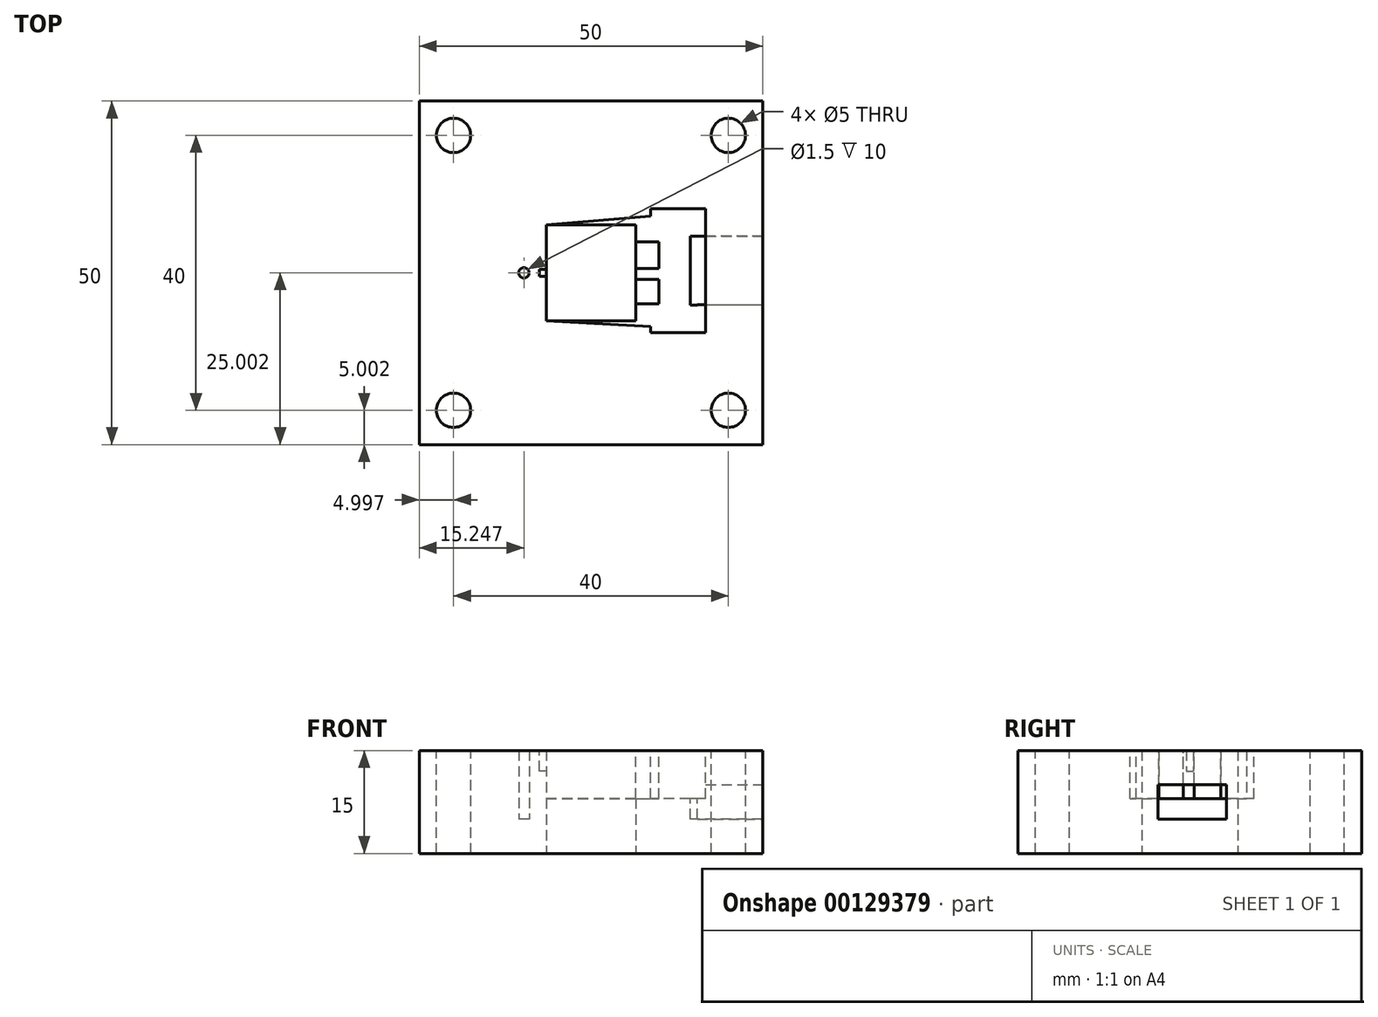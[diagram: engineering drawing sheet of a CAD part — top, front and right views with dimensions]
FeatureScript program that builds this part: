
annotation { "Feature Type Name" : "Feature", "Feature Type Description" : "" }
export const myFeature = defineFeature(function(context is Context, id is Id, definition is map)
    precondition{}
    {
        {
            var Q0;
            Q0=qCreatedBy(makeId("Top.planeOp"),FACE);
            var sketch = newSketch(context, id + "F0", { "sketchPlane" : qUnion([Q0])});
            skLineSegment(sketch, "E0.bottom", {"start": v(-16.2, 16.2) * mm, "end": v(23.8, 16.2) * mm});
            skLineSegment(sketch, "E0.top", {"start": v(-16.2, -23.8) * mm, "end": v(23.8, -23.8) * mm});
            skLineSegment(sketch, "E0.left", {"start": v(-16.2, 16.2) * mm, "end": v(-16.2, -23.8) * mm});
            skLineSegment(sketch, "E0.right", {"start": v(23.8, 16.2) * mm, "end": v(23.8, -23.8) * mm});
            skLineSegment(sketch, "E1", {"start": v(3.8, 16.2) * mm, "end": v(3.8, -23.8) * mm, "construction": true});
            skLineSegment(sketch, "E2", {"start": v(-16.2, -3.8) * mm, "end": v(23.8, -3.8) * mm, "construction": true});
            skLineSegment(sketch, "E3.bottom", {"start": v(10.3, -10.8) * mm, "end": v(-2.7, -10.8) * mm});
            skLineSegment(sketch, "E3.top", {"start": v(10.3, 3.2) * mm, "end": v(-2.7, 3.2) * mm});
            skLineSegment(sketch, "E3.left", {"start": v(10.3, -10.8) * mm, "end": v(10.3, 3.2) * mm});
            skLineSegment(sketch, "E3.right", {"start": v(-2.7, -10.8) * mm, "end": v(-2.7, 3.2) * mm});
            skPoint(sketch, "E3.middle", {"position": v(3.8, -3.8) * mm});
            skCircle(sketch, "E4", {"center": v(-5.95, -3.8) * mm, "radius": 0.75 * mm});
            skSolve(sketch);
        }
        {
            var Q0;
            Q0 = qSketchRegion(id + "F0", true);
            extrude(context, id + "F1", {"entities" : qUnion([Q0]), "depth" : 10 * mm});
        }
        {
            var Q0;
            Q0=makeQuery(id+"F1.opExtrude","CAP_FACE",FACE,{"disambiguationData":[OSD([sQuery(id+"F0.wireOp",EDGE,"E0.bottom"),sQuery(id+"F0.wireOp",EDGE,"E0.top"),sQuery(id+"F0.wireOp",EDGE,"E0.left"),sQuery(id+"F0.wireOp",EDGE,"E0.right"),sQuery(id+"F0.wireOp",EDGE,"E3.bottom"),sQuery(id+"F0.wireOp",EDGE,"E3.top"),sQuery(id+"F0.wireOp",EDGE,"E3.left"),sQuery(id+"F0.wireOp",EDGE,"E3.right")])],"isStart":false});
            var sketch = newSketch(context, id + "F2", { "sketchPlane" : qUnion([Q0])});
            skLineSegment(sketch, "E5", {"start": v(-2.7, -10.8) * mm, "end": v(19.32, -11.97) * mm});
            skLineSegment(sketch, "E6", {"start": v(-2.7, 3.2) * mm, "end": v(19.27, 5.03) * mm});
            skLineSegment(sketch, "E7", {"start": v(19.27, 5.03) * mm, "end": v(19.32, -11.97) * mm});
            skLineSegment(sketch, "E8", {"start": v(10.3, -1.44) * mm, "end": v(14.3, -1.44) * mm});
            skLineSegment(sketch, "E9", {"start": v(10.3, -5.36) * mm, "end": v(14.12, -5.36) * mm});
            skLineSegment(sketch, "E10", {"start": v(14.3, -5.36) * mm, "end": v(14.3, -1.44) * mm});
            skPoint(sketch, "E11.endSnap0", {"position": v(19.3, -3.47) * mm});
            skLineSegment(sketch, "E12", {"start": v(10.3, -1.44) * mm, "end": v(10.3, -5.36) * mm});
            skLineSegment(sketch, "E13", {"start": v(-2.7, -10.8) * mm, "end": v(-2.7, 3.2) * mm});
            skSolve(sketch);
        }
        {
            var Q0;
            Q0=makeQuery(id+"F2.imprint","IMPRINT",FACE,{"disambiguationData":[TD([[makeQuery(id+"F2.imprint","IMPRINT",EDGE,{"derivedFrom":sQuery(id+"F2.wireOp",EDGE,"E5")}),1.0]])]});
            extrude(context, id + "F3", {"entities" : qUnion([Q0]), "operationType" : NewBodyOperationType.REMOVE, "oppositeDirection" : true, "depth" : 7 * mm});
        }
        {
            var Q0;
            Q0=makeQuery(id+"F3.boolean.opBoolean","COPY",FACE,{"derivedFrom":makeQuery(id+"F3.opExtrude","CAP_FACE",FACE,{"disambiguationData":[OSD([sQuery(id+"F0.wireOp",EDGE,"E3.bottom"),sQuery(id+"F0.wireOp",EDGE,"E3.top"),sQuery(id+"F0.wireOp",EDGE,"E3.left"),sQuery(id+"F2.wireOp",EDGE,"E5"),sQuery(id+"F2.wireOp",EDGE,"E6"),sQuery(id+"F2.wireOp",EDGE,"E7"),sQuery(id+"F2.wireOp",EDGE,"E12")])],"isStart":false})});
            var sketch = newSketch(context, id + "F4", { "sketchPlane" : qUnion([Q0])});
            skLineSegment(sketch, "E14.top", {"start": v(10.3, -8.3) * mm, "end": v(14.3, -8.3) * mm});
            skLineSegment(sketch, "E15.top", {"start": v(10.3, 0.7) * mm, "end": v(14.3, 0.7) * mm});
            skLineSegment(sketch, "E16", {"start": v(14.3, -8.3) * mm, "end": v(14.3, 0.7) * mm});
            skLineSegment(sketch, "E17", {"start": v(10.3, -3.8) * mm, "end": v(38.3, -3.8) * mm, "construction": true});
            skLineSegment(sketch, "E18", {"start": v(10.3, -3.8) * mm, "end": v(10.3, 0.7) * mm});
            skLineSegment(sketch, "E19", {"start": v(10.3, -3.8) * mm, "end": v(10.3, -8.3) * mm});
            skSolve(sketch);
        }
        {
            var Q0;
            Q0 = qSketchRegion(id + "F4", true);
            extrude(context, id + "F5", {"entities" : qUnion([Q0]), "operationType" : NewBodyOperationType.ADD, "depth" : 7 * mm});
        }
        {
            var Q0;
            Q0=makeQuery(id+"F3.boolean.opBoolean","COPY",FACE,{"derivedFrom":makeQuery(id+"F3.opExtrude","CAP_FACE",FACE,{"disambiguationData":[OSD([sQuery(id+"F0.wireOp",EDGE,"E3.bottom"),sQuery(id+"F0.wireOp",EDGE,"E3.top"),sQuery(id+"F0.wireOp",EDGE,"E3.left"),sQuery(id+"F2.wireOp",EDGE,"E5"),sQuery(id+"F2.wireOp",EDGE,"E6"),sQuery(id+"F2.wireOp",EDGE,"E7"),sQuery(id+"F2.wireOp",EDGE,"E12")])],"isStart":false})});
            var sketch = newSketch(context, id + "F6", { "sketchPlane" : qUnion([Q0])});
            skLineSegment(sketch, "E20.top", {"start": v(19.27, 1.53) * mm, "end": v(18.27, 1.53) * mm});
            skLineSegment(sketch, "E21.top", {"start": v(19.27, -8.47) * mm, "end": v(18.27, -8.47) * mm});
            skLineSegment(sketch, "E22", {"start": v(18.27, 1.53) * mm, "end": v(18.27, -8.47) * mm});
            skLineSegment(sketch, "E23", {"start": v(19.27, -8.47) * mm, "end": v(19.27, 1.53) * mm});
            skSolve(sketch);
        }
        {
            var Q0;
            Q0 = qSketchRegion(id + "F6", true);
            extrude(context, id + "F7", {"entities" : qUnion([Q0]), "operationType" : NewBodyOperationType.REMOVE, "oppositeDirection" : true, "depth" : 3 * mm});
        }
        {
            var Q0;
            Q0=makeQuery(id+"F1.opExtrude","CAP_FACE",FACE,{"disambiguationData":[OSD([sQuery(id+"F0.wireOp",EDGE,"E0.bottom"),sQuery(id+"F0.wireOp",EDGE,"E0.top"),sQuery(id+"F0.wireOp",EDGE,"E0.left"),sQuery(id+"F0.wireOp",EDGE,"E0.right"),sQuery(id+"F0.wireOp",EDGE,"E3.bottom"),sQuery(id+"F0.wireOp",EDGE,"E3.top"),sQuery(id+"F0.wireOp",EDGE,"E3.left"),sQuery(id+"F0.wireOp",EDGE,"E3.right")])],"isStart":true});
            var sketch = newSketch(context, id + "F8", { "sketchPlane" : qUnion([Q0])});
            skLineSegment(sketch, "E24.bottom", {"start": v(18.27, -1.53) * mm, "end": v(35.19, -1.53) * mm});
            skLineSegment(sketch, "E24.top", {"start": v(18.27, 8.45) * mm, "end": v(35.19, 8.45) * mm});
            skLineSegment(sketch, "E24.left", {"start": v(18.27, -1.53) * mm, "end": v(18.27, 8.45) * mm});
            skLineSegment(sketch, "E24.right", {"start": v(35.19, -1.53) * mm, "end": v(35.19, 8.45) * mm});
            skSolve(sketch);
        }
        {
            var Q0;
            Q0=makeQuery(id+"F1.opExtrude","CAP_FACE",FACE,{"disambiguationData":[OSD([sQuery(id+"F0.wireOp",EDGE,"E0.bottom"),sQuery(id+"F0.wireOp",EDGE,"E0.top"),sQuery(id+"F0.wireOp",EDGE,"E0.left"),sQuery(id+"F0.wireOp",EDGE,"E0.right"),sQuery(id+"F0.wireOp",EDGE,"E3.bottom"),sQuery(id+"F0.wireOp",EDGE,"E3.top"),sQuery(id+"F0.wireOp",EDGE,"E3.left"),sQuery(id+"F0.wireOp",EDGE,"E3.right")])],"isStart":true});
            var sketch = newSketch(context, id + "F9", { "sketchPlane" : qUnion([Q0])});
            skLineSegment(sketch, "E25.bottom", {"start": v(-16.2, 23.8) * mm, "end": v(23.8, 23.8) * mm});
            skLineSegment(sketch, "E25.top", {"start": v(-16.2, -16.2) * mm, "end": v(23.8, -16.2) * mm});
            skLineSegment(sketch, "E25.left", {"start": v(-16.2, 23.8) * mm, "end": v(-16.2, -16.2) * mm});
            skLineSegment(sketch, "E25.right", {"start": v(23.8, 23.8) * mm, "end": v(23.8, -16.2) * mm});
            skLineSegment(sketch, "E26.bottom", {"start": v(-2.7, 10.8) * mm, "end": v(10.3, 10.8) * mm});
            skLineSegment(sketch, "E26.top", {"start": v(-2.7, -3.2) * mm, "end": v(10.3, -3.2) * mm});
            skLineSegment(sketch, "E26.left", {"start": v(-2.7, 10.8) * mm, "end": v(-2.7, -3.2) * mm});
            skLineSegment(sketch, "E26.right", {"start": v(10.3, 10.8) * mm, "end": v(10.3, -3.2) * mm});
            skSolve(sketch);
        }
        {
            var Q0;
            Q0 = qSketchRegion(id + "F9", true);
            extrude(context, id + "F10", {"entities" : qUnion([Q0]), "operationType" : NewBodyOperationType.ADD, "depth" : 5 * mm});
        }
        {
            var Q0;
            Q0 = qSketchRegion(id + "F8", true);
            extrude(context, id + "F11", {"entities" : qUnion([Q0]), "operationType" : NewBodyOperationType.REMOVE, "oppositeDirection" : true, "depth" : 5 * mm});
        }
        {
            var Q0;
            Q0=makeQuery(id+"F1.opExtrude","CAP_FACE",FACE,{"disambiguationData":[OSD([sQuery(id+"F0.wireOp",EDGE,"E0.bottom"),sQuery(id+"F0.wireOp",EDGE,"E0.top"),sQuery(id+"F0.wireOp",EDGE,"E0.left"),sQuery(id+"F0.wireOp",EDGE,"E0.right"),sQuery(id+"F0.wireOp",EDGE,"E3.bottom"),sQuery(id+"F0.wireOp",EDGE,"E3.top"),sQuery(id+"F0.wireOp",EDGE,"E3.left"),sQuery(id+"F0.wireOp",EDGE,"E3.right")])],"isStart":false});
            var sketch = newSketch(context, id + "F12", { "sketchPlane" : qUnion([Q0])});
            skSolve(sketch);
        }
        {
            var Q0;
            Q0=makeQuery(id+"F12.imprint","IMPRINT",FACE,{"disambiguationData":[TD([[makeQuery(id+"F12.imprint","IMPRINT",EDGE,{"derivedFrom":makeQuery(id+"F1.opExtrude","CAP_EDGE",EDGE,{"disambiguationData":[OSD([sQuery(id+"F0.wireOp",EDGE,"E0.bottom")])],"isStart":false})}),-1.0]])]});
            var sketch = newSketch(context, id + "F13", { "sketchPlane" : qUnion([Q0])});
            skLineSegment(sketch, "E27.bottom", {"start": v(19.5, 5.53) * mm, "end": v(15.5, 5.53) * mm});
            skLineSegment(sketch, "E27.top", {"start": v(19.5, -12.47) * mm, "end": v(15.5, -12.47) * mm});
            skLineSegment(sketch, "E27.left", {"start": v(19.5, 5.53) * mm, "end": v(19.5, -12.47) * mm});
            skLineSegment(sketch, "E27.right", {"start": v(15.5, 5.53) * mm, "end": v(15.5, -12.47) * mm});
            skLineSegment(sketch, "E28.bottom", {"start": v(15.5, 5.53) * mm, "end": v(12.5, 5.53) * mm});
            skLineSegment(sketch, "E28.top", {"start": v(15.5, 3.72) * mm, "end": v(12.5, 3.72) * mm});
            skLineSegment(sketch, "E28.left", {"start": v(15.5, 5.53) * mm, "end": v(15.5, 3.72) * mm});
            skLineSegment(sketch, "E28.right", {"start": v(12.5, 5.53) * mm, "end": v(12.5, 3.72) * mm});
            skLineSegment(sketch, "E29.bottom", {"start": v(15.5, -12.47) * mm, "end": v(12.5, -12.47) * mm});
            skLineSegment(sketch, "E29.top", {"start": v(15.5, -10.8) * mm, "end": v(12.5, -10.8) * mm});
            skLineSegment(sketch, "E29.left", {"start": v(15.5, -12.47) * mm, "end": v(15.5, -10.8) * mm});
            skLineSegment(sketch, "E29.right", {"start": v(12.5, -12.47) * mm, "end": v(12.5, -10.8) * mm});
            skSolve(sketch);
        }
        {
            var Q0;
            Q0 = qSketchRegion(id + "F13", true);
            extrude(context, id + "F14", {"entities" : qUnion([Q0]), "operationType" : NewBodyOperationType.REMOVE, "oppositeDirection" : true, "depth" : 7 * mm});
        }
        {
            var Q0;
            Q0=qCreatedBy(makeId("Top.planeOp"),FACE);
            var sketch = newSketch(context, id + "F15", { "sketchPlane" : qUnion([Q0])});
            skLineSegment(sketch, "E30.bottom", {"start": v(-21.2, 21.2) * mm, "end": v(28.8, 21.2) * mm});
            skLineSegment(sketch, "E30.top", {"start": v(-21.2, -28.8) * mm, "end": v(28.8, -28.8) * mm});
            skLineSegment(sketch, "E30.left", {"start": v(-21.2, 21.2) * mm, "end": v(-21.2, -28.8) * mm});
            skLineSegment(sketch, "E30.right", {"start": v(28.8, 21.2) * mm, "end": v(28.8, -28.8) * mm});
            skLineSegment(sketch, "E31.bottom", {"start": v(-16.2, 16.2) * mm, "end": v(23.8, 16.2) * mm});
            skLineSegment(sketch, "E31.top", {"start": v(-16.2, -23.8) * mm, "end": v(23.8, -23.8) * mm});
            skLineSegment(sketch, "E31.left", {"start": v(-16.2, 16.2) * mm, "end": v(-16.2, -23.8) * mm});
            skLineSegment(sketch, "E31.right", {"start": v(23.8, 16.2) * mm, "end": v(23.8, -23.8) * mm});
            skSolve(sketch);
        }
        {
            var Q0;
            Q0 = qSketchRegion(id + "F15", true);
            extrude(context, id + "F16", {"entities" : qUnion([Q0]), "operationType" : NewBodyOperationType.ADD, "depth" : 10 * mm, "hasSecondDirection" : true, "secondDirectionOppositeDirection" : true, "secondDirectionDepth" : 5 * mm});
        }
        {
            var Q0;
            Q0=makeQuery(id+"F12.imprint","IMPRINT",FACE,{"disambiguationData":[TD([[makeQuery(id+"F12.imprint","IMPRINT",EDGE,{"derivedFrom":makeQuery(id+"F1.opExtrude","CAP_EDGE",EDGE,{"disambiguationData":[OSD([sQuery(id+"F0.wireOp",EDGE,"E0.bottom")])],"isStart":false})}),-1.0]])]});
            var sketch = newSketch(context, id + "F17", { "sketchPlane" : qUnion([Q0])});
            skLineSegment(sketch, "E32.bottom", {"start": v(-21.2, 21.2) * mm, "end": v(28.8, 21.2) * mm, "construction": true});
            skLineSegment(sketch, "E32.top", {"start": v(-21.2, -28.8) * mm, "end": v(28.8, -28.8) * mm, "construction": true});
            skLineSegment(sketch, "E32.left", {"start": v(-21.2, 21.2) * mm, "end": v(-21.2, -28.8) * mm, "construction": true});
            skLineSegment(sketch, "E32.right", {"start": v(28.8, 21.2) * mm, "end": v(28.8, -28.8) * mm, "construction": true});
            skLineSegment(sketch, "E33", {"start": v(-21.2, 21.2) * mm, "end": v(28.8, -28.8) * mm, "construction": true});
            skLineSegment(sketch, "E34", {"start": v(28.8, 21.2) * mm, "end": v(-21.2, -28.8) * mm, "construction": true});
            skCircle(sketch, "E35", {"center": v(-16.2, -23.8) * mm, "radius": 2.5 * mm});
            skCircle(sketch, "E36.0.1.0", {"center": v(-16.2, 16.2) * mm, "radius": 2.5 * mm});
            skCircle(sketch, "E36.1.0.0", {"center": v(23.8, -23.8) * mm, "radius": 2.5 * mm});
            skCircle(sketch, "E36.1.1.0", {"center": v(23.8, 16.2) * mm, "radius": 2.5 * mm});
            skLineSegment(sketch, "E36.direction1", {"start": v(-16.2, -23.8) * mm, "end": v(23.8, -23.8) * mm, "construction": true});
            skLineSegment(sketch, "E36.direction2", {"start": v(-16.2, -23.8) * mm, "end": v(-16.2, 16.2) * mm, "construction": true});
            skSolve(sketch);
        }
        {
            var Q0;
            {var subQ3=sQuery(id+"F8.wireOp",EDGE,"E24.left");Q0=makeQuery(id+"F8.imprint","IMPRINT",FACE,{"disambiguationData":[TD([[makeQuery(id+"F8.imprint","IMPRINT",EDGE,{"derivedFrom":subQ3}),-1.0]])]});}
            var Q1;
            {var subQ0=sQuery(id+"F8.wireOp",EDGE,"E24.bottom");var subQ3=makeQuery(id+"F1.opExtrude","CAP_EDGE",EDGE,{"disambiguationData":[OSD([sQuery(id+"F0.wireOp",EDGE,"E0.right")])],"isStart":true});var subQ4=makeQuery(id+"F8.imprint","INTERSECT",VERTEX,{"derivedFrom":[subQ3,subQ0]});Q1=makeQuery(id+"F8.imprint","IMPRINT",FACE,{"disambiguationData":[TD([[makeQuery(id+"F8.imprint","IMPRINT",EDGE,{"disambiguationData":[TD([[subQ4,1.0]])],"derivedFrom":subQ0}),1.0]])]});}
            var Q2;
            {var subQ0=sQuery(id+"F8.wireOp",EDGE,"E24.right");Q2=makeQuery(id+"F8.imprint","IMPRINT",FACE,{"disambiguationData":[TD([[makeQuery(id+"F8.imprint","IMPRINT",EDGE,{"derivedFrom":subQ0}),1.0]])]});}
            extrude(context, id + "F18", {"entities" : qUnion([Q0, Q1, Q2]), "operationType" : NewBodyOperationType.REMOVE, "oppositeDirection" : true, "depth" : 5 * mm});
        }
        {
            var Q0;
            Q0 = qSketchRegion(id + "F17", true);
            extrude(context, id + "F19", {"entities" : qUnion([Q0]), "operationType" : NewBodyOperationType.REMOVE, "oppositeDirection" : true, "depth" : 15 * mm});
        }
        {
            var Q0;
            Q0=makeQuery(id+"F16.boolean.opBoolean","MERGE",FACE,{"derivedFrom":[makeQuery(id+"F1.opExtrude","CAP_FACE",FACE,{"disambiguationData":[OSD([sQuery(id+"F0.wireOp",EDGE,"E0.bottom"),sQuery(id+"F0.wireOp",EDGE,"E0.top"),sQuery(id+"F0.wireOp",EDGE,"E0.left"),sQuery(id+"F0.wireOp",EDGE,"E0.right"),sQuery(id+"F0.wireOp",EDGE,"E3.bottom"),sQuery(id+"F0.wireOp",EDGE,"E3.top"),sQuery(id+"F0.wireOp",EDGE,"E3.left"),sQuery(id+"F0.wireOp",EDGE,"E3.right"),sQuery(id+"F0.wireOp",EDGE,"E4")])],"isStart":false}),makeQuery(id+"F16.opExtrude","CAP_FACE",FACE,{"disambiguationData":[OSD([sQuery(id+"F15.wireOp",EDGE,"E30.bottom"),sQuery(id+"F15.wireOp",EDGE,"E30.top"),sQuery(id+"F15.wireOp",EDGE,"E30.left"),sQuery(id+"F15.wireOp",EDGE,"E30.right"),sQuery(id+"F15.wireOp",EDGE,"E31.bottom"),sQuery(id+"F15.wireOp",EDGE,"E31.top"),sQuery(id+"F15.wireOp",EDGE,"E31.left"),sQuery(id+"F15.wireOp",EDGE,"E31.right")])],"isStart":false})]});
            var sketch = newSketch(context, id + "F20", { "sketchPlane" : qUnion([Q0])});
            skLineSegment(sketch, "E37.bottom", {"start": v(19.5, 5.53) * mm, "end": v(20.5, 5.53) * mm});
            skLineSegment(sketch, "E37.top", {"start": v(19.5, -12.47) * mm, "end": v(20.5, -12.47) * mm});
            skLineSegment(sketch, "E37.left", {"start": v(19.5, 5.53) * mm, "end": v(19.5, -12.47) * mm});
            skLineSegment(sketch, "E37.right", {"start": v(20.5, 5.53) * mm, "end": v(20.5, -12.47) * mm});
            skLineSegment(sketch, "E38.bottom", {"start": v(13.67, 0.9) * mm, "end": v(14.77, 0.9) * mm});
            skLineSegment(sketch, "E38.top", {"start": v(13.67, -8.78) * mm, "end": v(14.77, -8.78) * mm});
            skLineSegment(sketch, "E38.left", {"start": v(13.67, 0.9) * mm, "end": v(13.67, -8.78) * mm});
            skLineSegment(sketch, "E38.right", {"start": v(14.77, 0.9) * mm, "end": v(14.77, -8.78) * mm});
            skLineSegment(sketch, "E39.bottom", {"start": v(10.22, -3.14) * mm, "end": v(14.77, -3.14) * mm});
            skLineSegment(sketch, "E39.top", {"start": v(10.22, -4.76) * mm, "end": v(14.77, -4.76) * mm});
            skLineSegment(sketch, "E39.left", {"start": v(10.22, -3.14) * mm, "end": v(10.22, -4.76) * mm});
            skLineSegment(sketch, "E39.right", {"start": v(14.77, -3.14) * mm, "end": v(14.77, -4.76) * mm});
            skSolve(sketch);
        }
        {
            var Q0;
            Q0 = qSketchRegion(id + "F20", true);
            extrude(context, id + "F21", {"entities" : qUnion([Q0]), "operationType" : NewBodyOperationType.REMOVE, "oppositeDirection" : true, "depth" : 7 * mm});
        }
        {
            var Q0;
            Q0=makeQuery(id+"F16.boolean.opBoolean","MERGE",FACE,{"derivedFrom":[makeQuery(id+"F1.opExtrude","CAP_FACE",FACE,{"disambiguationData":[OSD([sQuery(id+"F0.wireOp",EDGE,"E0.bottom"),sQuery(id+"F0.wireOp",EDGE,"E0.top"),sQuery(id+"F0.wireOp",EDGE,"E0.left"),sQuery(id+"F0.wireOp",EDGE,"E0.right"),sQuery(id+"F0.wireOp",EDGE,"E3.bottom"),sQuery(id+"F0.wireOp",EDGE,"E3.top"),sQuery(id+"F0.wireOp",EDGE,"E3.left"),sQuery(id+"F0.wireOp",EDGE,"E3.right"),sQuery(id+"F0.wireOp",EDGE,"E4")])],"isStart":false}),makeQuery(id+"F16.opExtrude","CAP_FACE",FACE,{"disambiguationData":[OSD([sQuery(id+"F15.wireOp",EDGE,"E30.bottom"),sQuery(id+"F15.wireOp",EDGE,"E30.top"),sQuery(id+"F15.wireOp",EDGE,"E30.left"),sQuery(id+"F15.wireOp",EDGE,"E30.right"),sQuery(id+"F15.wireOp",EDGE,"E31.bottom"),sQuery(id+"F15.wireOp",EDGE,"E31.top"),sQuery(id+"F15.wireOp",EDGE,"E31.left"),sQuery(id+"F15.wireOp",EDGE,"E31.right")])],"isStart":false})]});
            var sketch = newSketch(context, id + "F22", { "sketchPlane" : qUnion([Q0])});
            skLineSegment(sketch, "E40.bottom", {"start": v(-1.72, -4.3) * mm, "end": v(-3.68, -4.3) * mm});
            skLineSegment(sketch, "E40.top", {"start": v(-1.72, -3.3) * mm, "end": v(-3.68, -3.3) * mm});
            skLineSegment(sketch, "E40.left", {"start": v(-1.72, -4.3) * mm, "end": v(-1.72, -3.3) * mm});
            skLineSegment(sketch, "E40.right", {"start": v(-3.68, -4.3) * mm, "end": v(-3.68, -3.3) * mm});
            skPoint(sketch, "E40.middle", {"position": v(-2.7, -3.8) * mm});
            skSolve(sketch);
        }
        {
            var Q0;
            Q0 = qSketchRegion(id + "F22", true);
            extrude(context, id + "F23", {"entities" : qUnion([Q0]), "operationType" : NewBodyOperationType.REMOVE, "oppositeDirection" : true, "depth" : 3 * mm});
        }
    });
